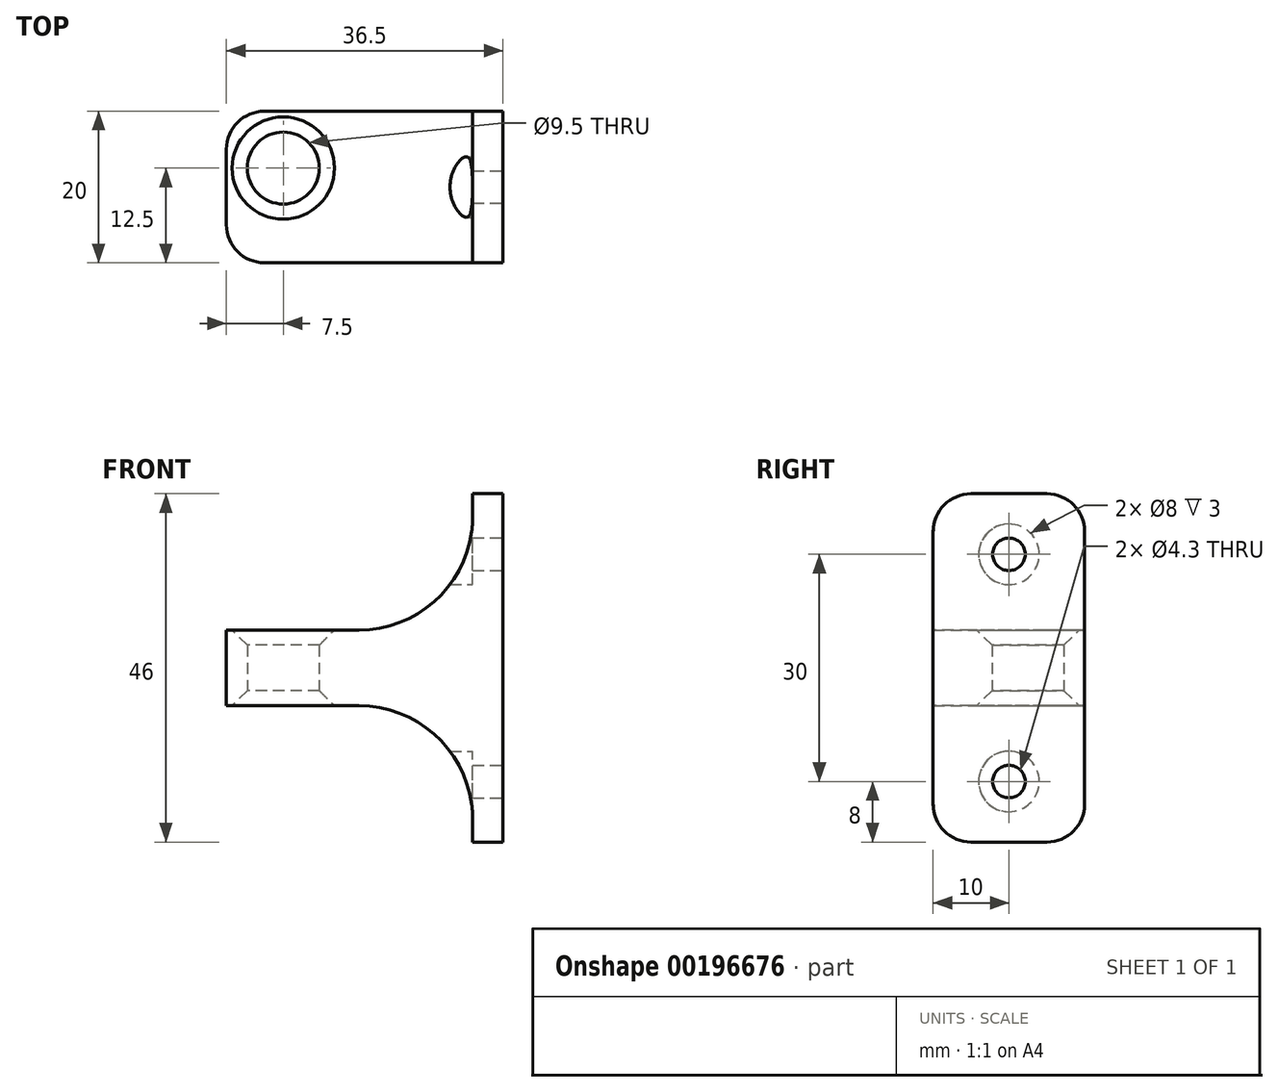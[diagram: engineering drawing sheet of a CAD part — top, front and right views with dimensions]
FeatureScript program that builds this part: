
annotation { "Feature Type Name" : "Feature", "Feature Type Description" : "" }
export const myFeature = defineFeature(function(context is Context, id is Id, definition is map)
    precondition{}
    {
        {
            var Q0;
            Q0=qCreatedBy(makeId("Top.planeOp"),FACE);
            var sketch = newSketch(context, id + "F0", { "sketchPlane" : qUnion([Q0])});
            skCircle(sketch, "E0", {"center": v(-29, 0) * mm, "radius": 4.75 * mm});
            skLineSegment(sketch, "E1.bottom", {"start": v(-36.5, 7.5) * mm, "end": v(0, 7.5) * mm});
            skLineSegment(sketch, "E1.top", {"start": v(-36.5, -12.5) * mm, "end": v(0, -12.5) * mm});
            skLineSegment(sketch, "E1.left", {"start": v(-36.5, 7.5) * mm, "end": v(-36.5, -12.5) * mm});
            skLineSegment(sketch, "E1.right", {"start": v(0, 7.5) * mm, "end": v(0, -12.5) * mm});
            skSolve(sketch);
        }
        {
            var Q0;
            Q0=makeQuery(id+"F0.imprint","IMPRINT",FACE,{"disambiguationData":[TD([[makeQuery(id+"F0.imprint","IMPRINT",EDGE,{"derivedFrom":sQuery(id+"F0.wireOp",EDGE,"E0")}),-1.0]])]});
            extrude(context, id + "F1", {"entities" : qUnion([Q0]), "depth" : 5 * mm, "hasSecondDirection" : true, "secondDirectionOppositeDirection" : true, "secondDirectionDepth" : 5 * mm});
        }
        {
            var Q0;
            Q0=makeQuery(id+"F1.opExtrude","CAP_EDGE",EDGE,{"disambiguationData":[OSD([sQuery(id+"F0.wireOp",EDGE,"E0")])],"isStart":false});
            var Q1;
            Q1=makeQuery(id+"F1.opExtrude","CAP_EDGE",EDGE,{"disambiguationData":[OSD([sQuery(id+"F0.wireOp",EDGE,"E0")])],"isStart":true});
            chamfer(context, id + "F2", {"entities" : qUnion([Q0, Q1]), "width" : 2 * mm, "tangentPropagation" : true});
        }
        {
            var Q0;
            Q0=qCreatedBy(makeId("Right.planeOp"),FACE);
            var sketch = newSketch(context, id + "F3", { "sketchPlane" : qUnion([Q0])});
            skLineSegment(sketch, "E2.bottom", {"start": v(-12.5, 23) * mm, "end": v(7.5, 23) * mm});
            skLineSegment(sketch, "E2.top", {"start": v(-12.5, -23) * mm, "end": v(7.5, -23) * mm});
            skLineSegment(sketch, "E2.left", {"start": v(-12.5, 23) * mm, "end": v(-12.5, -23) * mm});
            skLineSegment(sketch, "E2.right", {"start": v(7.5, 23) * mm, "end": v(7.5, -23) * mm});
            skCircle(sketch, "E3", {"center": v(-2.5, 15) * mm, "radius": 2.15 * mm});
            skCircle(sketch, "E4", {"center": v(-2.5, -15) * mm, "radius": 2.15 * mm});
            skCircle(sketch, "E5", {"center": v(-2.5, 15) * mm, "radius": 4 * mm});
            skCircle(sketch, "E6", {"center": v(-2.5, -15) * mm, "radius": 4 * mm});
            skSolve(sketch);
        }
        {
            var Q0;
            Q0=makeQuery(id+"F3.imprint","IMPRINT",FACE,{"disambiguationData":[TD([[makeQuery(id+"F3.imprint","IMPRINT",EDGE,{"derivedFrom":sQuery(id+"F3.wireOp",EDGE,"E2.bottom")}),-1.0]])]});
            extrude(context, id + "F4", {"entities" : qUnion([Q0]), "operationType" : NewBodyOperationType.ADD, "oppositeDirection" : true, "depth" : 4 * mm});
        }
        {
            var Q0;
            Q0=makeQuery(id+"F4.boolean.opBoolean","INTERSECT",EDGE,{"derivedFrom":[makeQuery(id+"F1.opExtrude","CAP_FACE",FACE,{"disambiguationData":[OSD([sQuery(id+"F0.wireOp",EDGE,"E0"),sQuery(id+"F0.wireOp",EDGE,"E1.bottom"),sQuery(id+"F0.wireOp",EDGE,"E1.top"),sQuery(id+"F0.wireOp",EDGE,"E1.left"),sQuery(id+"F0.wireOp",EDGE,"E1.right")])],"isStart":false}),makeQuery(id+"F4.opExtrude","CAP_FACE",FACE,{"disambiguationData":[OSD([sQuery(id+"F3.wireOp",EDGE,"E2.bottom"),sQuery(id+"F3.wireOp",EDGE,"E2.top"),sQuery(id+"F3.wireOp",EDGE,"E2.left"),sQuery(id+"F3.wireOp",EDGE,"E2.right"),sQuery(id+"F3.wireOp",EDGE,"E3"),sQuery(id+"F3.wireOp",EDGE,"E4")])],"isStart":false})]});
            var Q1;
            Q1=makeQuery(id+"F4.boolean.opBoolean","INTERSECT",EDGE,{"derivedFrom":[makeQuery(id+"F1.opExtrude","CAP_FACE",FACE,{"disambiguationData":[OSD([sQuery(id+"F0.wireOp",EDGE,"E0"),sQuery(id+"F0.wireOp",EDGE,"E1.bottom"),sQuery(id+"F0.wireOp",EDGE,"E1.top"),sQuery(id+"F0.wireOp",EDGE,"E1.left"),sQuery(id+"F0.wireOp",EDGE,"E1.right")])],"isStart":true}),makeQuery(id+"F4.opExtrude","CAP_FACE",FACE,{"disambiguationData":[OSD([sQuery(id+"F3.wireOp",EDGE,"E2.bottom"),sQuery(id+"F3.wireOp",EDGE,"E2.top"),sQuery(id+"F3.wireOp",EDGE,"E2.left"),sQuery(id+"F3.wireOp",EDGE,"E2.right"),sQuery(id+"F3.wireOp",EDGE,"E3"),sQuery(id+"F3.wireOp",EDGE,"E4")])],"isStart":false})]});
            fillet(context, id + "F5", {"entities" : qUnion([Q0, Q1]), "radius" : 15 * mm, "tangentPropagation" : true, "allowEdgeOverflow" : false});
        }
        {
            var Q0;
            Q0=makeQuery(id+"F3.imprint","IMPRINT",FACE,{"disambiguationData":[TD([[makeQuery(id+"F3.imprint","IMPRINT",EDGE,{"derivedFrom":sQuery(id+"F3.wireOp",EDGE,"E3")}),-1.0]])]});
            var Q1;
            Q1=makeQuery(id+"F3.imprint","IMPRINT",FACE,{"disambiguationData":[TD([[makeQuery(id+"F3.imprint","IMPRINT",EDGE,{"derivedFrom":sQuery(id+"F3.wireOp",EDGE,"E4")}),-1.0]])]});
            extrude(context, id + "F6", {"entities" : qUnion([Q0, Q1]), "operationType" : NewBodyOperationType.ADD, "oppositeDirection" : true, "depth" : 4 * mm});
        }
        {
            var Q0;
            Q0=makeQuery(id+"F4.opExtrude","SWEPT_EDGE",EDGE,{"disambiguationData":[OSD([sQuery(id+"F3.wireOp",EDGE,"E2.top"),sQuery(id+"F3.wireOp",EDGE,"E2.left")])]});
            var Q1;
            Q1=makeQuery(id+"F4.opExtrude","SWEPT_EDGE",EDGE,{"disambiguationData":[OSD([sQuery(id+"F3.wireOp",EDGE,"E2.bottom"),sQuery(id+"F3.wireOp",EDGE,"E2.left")])]});
            var Q2;
            Q2=makeQuery(id+"F4.opExtrude","SWEPT_EDGE",EDGE,{"disambiguationData":[OSD([sQuery(id+"F3.wireOp",EDGE,"E2.top"),sQuery(id+"F3.wireOp",EDGE,"E2.right")])]});
            var Q3;
            Q3=makeQuery(id+"F4.opExtrude","SWEPT_EDGE",EDGE,{"disambiguationData":[OSD([sQuery(id+"F3.wireOp",EDGE,"E2.bottom"),sQuery(id+"F3.wireOp",EDGE,"E2.right")])]});
            fillet(context, id + "F7", {"entities" : qUnion([Q0, Q1, Q2, Q3]), "radius" : 5 * mm, "tangentPropagation" : true, "allowEdgeOverflow" : false});
        }
        {
            var Q0;
            Q0=makeQuery(id+"F1.opExtrude","SWEPT_EDGE",EDGE,{"disambiguationData":[OSD([sQuery(id+"F0.wireOp",EDGE,"E1.top"),sQuery(id+"F0.wireOp",EDGE,"E1.left")])]});
            var Q1;
            Q1=makeQuery(id+"F1.opExtrude","SWEPT_EDGE",EDGE,{"disambiguationData":[OSD([sQuery(id+"F0.wireOp",EDGE,"E1.bottom"),sQuery(id+"F0.wireOp",EDGE,"E1.left")])]});
            fillet(context, id + "F8", {"entities" : qUnion([Q0, Q1]), "radius" : 5 * mm, "tangentPropagation" : true, "allowEdgeOverflow" : false});
        }
    });
